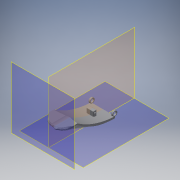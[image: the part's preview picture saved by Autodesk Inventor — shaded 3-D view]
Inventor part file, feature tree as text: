
AUTODESK INVENTOR PART (.ipt)
format: ipt  version: 2019 (Build 230136000, 136)  size: 14,473,216 bytes
history: native  units: in
note: dims shown in document units (in); Inventor stores cm internally (conversion verified against a paired STEP export)
features: other x7, extrude x6, sketch x6, reference x5, plane x3, fillet x1
ambient origin geometry x8: Origin, YZ Plane, XZ Plane, XY Plane, X Axis, Y Axis, Z Axis, Center Point
bodies: Solid1 (feature_tree)
feature tree (28):
  other  "Glyptodon Reduced 3.ipt"
  plane  "Work Plane1"
  extrude  "Extrusion1"  Depth=0.0197in
  extrude  "Extrusion2"  Depth=6.0in TaperAngle=0.0deg
  plane  "Work Plane2"
  extrude  "Extrusion3"  Depth=0.0197in
  extrude  "Extrusion6"  Depth=0.15in
  extrude  "Extrusion7"  Depth=0.1in TaperAngle=0.0deg
  plane  "Work Plane3"
  extrude  "Extrusion8"  Depth=0.0394in
  fillet  "Fillet1"  Radius=0.118in
  other  "Solid1::Glyptodon Reduced 3.ipt"
  other  "TaggingFeature1"
  sketch  "Sketch1"  dims[d0=0.0077in d1=0.0197in]
  reference  "Reference1"
  reference  "Reference2"
  reference  "Reference3"
  reference  "Reference4"
  reference  "Reference5"
  sketch  "Sketch2"  dims[d2=7.0in d3=0.0in d4=6.0in d5=0.0in]
  sketch  "Sketch3"  dims[d7=6.0in d8=0.0in d17=0.0197in]
  sketch  "Sketch6"  dims[d18=0.118in d19=0.15in]
  sketch  "Sketch7"  dims[d20=0.1in d21=0.0in d22=0.1in d23=0.0in]
  sketch  "Sketch8"  dims[d24=0.236in d25=0.118in d26=0.118in d27=0.118in d28=0.524in d29=0.0in d30=0.0394in]
  parser-record x1  (decoder bookkeeping rows leaked as tree rows — omitted from the tree; the rows remain in map.json)
  other  "Head Assemble.iam"
  other  "Head Workable With Mouth:1"
  other  "<userpath>\Documents\Inventor\Glyptodon Head\Head Assemble.iam"
note: 1 file-system path scrubbed to <path> (originals preserved in map.json)
